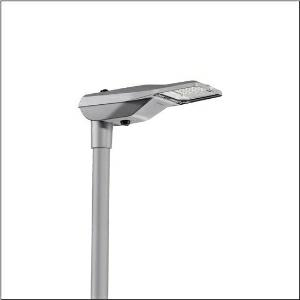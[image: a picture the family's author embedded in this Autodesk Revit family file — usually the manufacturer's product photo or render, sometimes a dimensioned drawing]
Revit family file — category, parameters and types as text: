
# Revit family: streetlight_sl_21_iq_micro___p0_8ab_5xe1r31y08db_c2fe
name_source: partatom
category: Lighting Fixtures
units: mm (PartAtom-declared; Revit-internal decimal feet)

## family parameters
Cut with Voids When Loaded = No
Host = Face
Light Source = No
Part Type = Normal
Room Calculation Point = No
Round Connector Dimension = Use Diameter
Shared = No

## types (1)
- --- (1 x LED, 4550 lm, 39.1 W, 3000K)
    Apparent Load = 39 VA
    CIE Flux Codes = 36 71 98 100 100
    Color Rendering = 70
    Color Temperature = 3000K
    Default Elevation = 1800 mm
    Description = Streetlight SL 21 iQ micro, mast luminaire, primary light control with lens, of PMMA, primary optical cover: cover, of toughened safety glass, transparent, light distribution: P0.8aB, light emission: direct distribution, primary light characteristic: asymmetric, installation type: post-top, side-entry, LED, High Power LED, rated luminous flux: 4.550lm, luminous efficacy: 116lm/W, light colour: 730, colour temperature: 3000K, control gear: iQ-Street Remote, D4i with power reduction, control: pre-setting: logarithmic dimming characteristic, Street-Remote, Auto-Match, Temp-Guard, Lumen-Switch, Night-Set, Smart-Wire, Light-Fading, Desk-Remote (wireless, voltage-free reading and setting of iQ features in the workshop via application-optimized NFC function/RFID function), optimised constant luminous flux control (CLO 2.0), mains connection: 220..240V, AC, 50/60Hz, start of lifetime: 39W, end of service life: 41W, reduction: 17W, luminaire housing, of diecast aluminium, powder-coated, Siteco® metallic grey (DB 702S), corrosivity category C5 mid according to DIN EN ISO 12944, please order mast flange separately, inclination adjustable: 0°, 5°, 10°, 15°, sealing non-destructively replaceable, multi-level sealing system, length: 528mm, width: 235mm, height: 110mm, mast flange for spigot size: 42mm (side-entry): 5XC10008XM4, 60/48mm (side-entry/post-top): 5XC10108XM2, 76/60mm (side-entry/post-top): 5XC10108XM1, mounting height: 4..8m, Smart Interface below and above, protection rating (complete): IP66, insulation class (complete): insulation class II (safety insulation), certification: CE, ENEC, ENEC+, VDE, impact resistance: IK10, permissible operating ambient temperature for outdoor applications: -40..+50°C, standard-compliant lighting for roads and squares, packaging unit: 1 piece

Light Distribution: P0.8aB
    Height = 110 mm
    Lamp = 1 x LED
    Lamp Light Flux = 4550 lm
    Lamp Power = 39.1 W
    Lamp count = 1
    Length = 528 mm
    Luminous efficacy = 116 lm/W
    Manufacturer = Siteco
    ModVariant = No
    Model = 5XE1R31Y08DB
    Number of Poles = 1
    OnlyDefault = Yes
    Power Factor = 1
    Product Name = Streetlight SL 21 iQ micro | P0.8aB
    Product group = mast luminaire | pylon top
    ProductGroupID = 6100
    Protection Class = Protection class II
    Protection Degree = IP 66
    RLX_Detail_Level = 1
    RLX_Emergency_Light_Flux = 0 lm
    RLX_Emergency_Type = 0
    RLX_Emergency_Type_DB = No
    RlxData = <blob elided: 98813 chars, md5=883f26ea>
    Socket = socket
    Standby Power = 0 W
    System Light Flux = 4550 lm
    System Power = 39 W
    Type Comments = factory setting: luminous flux: 100 % | dim-lin: 254 | 765 mA
    Type Image = l_1007239.jpg
    URL = http://relux.com
    VarID = @adj_097067
    Voltage = 0 V
    Weight = 0.00 kg
    Width = 235 mm

## geometry (parser evidence)
native form markers: Blend x4, Sweep x11
no freeform markers — native parametric forms only
